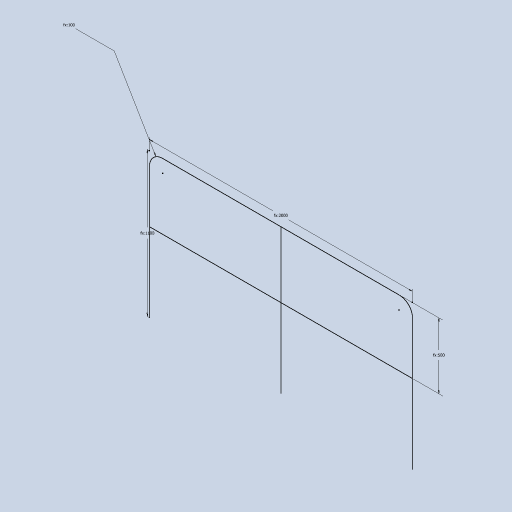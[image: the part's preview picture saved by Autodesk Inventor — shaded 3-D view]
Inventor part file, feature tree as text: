
AUTODESK INVENTOR PART (.ipt)
format: ipt  version: 2024.3 (Build 283343000, 343)  size: 82,432 bytes
history: native  units: mm
features: sketch x1
ambient origin geometry x8: Origin, YZ Plane, XZ Plane, XY Plane, X Axis, Y Axis, Z Axis, Center Point
feature tree (1):
  sketch  "Sketch4"  dims[d25=1100.0mm d26=2000.0mm d27=100.0mm]
